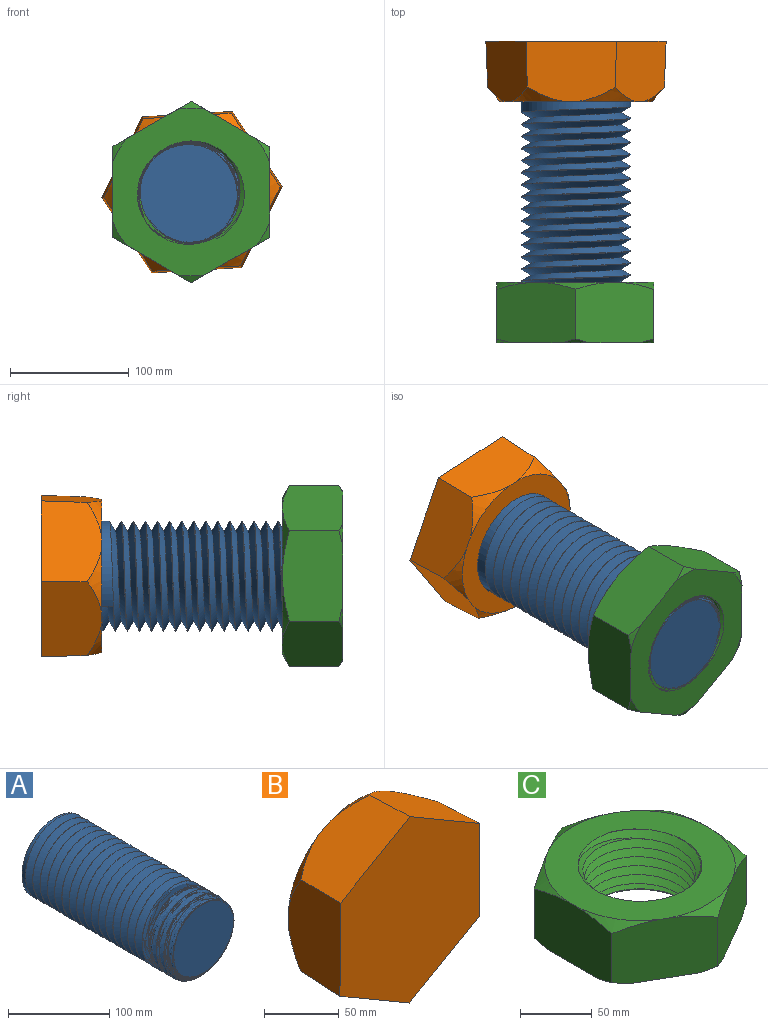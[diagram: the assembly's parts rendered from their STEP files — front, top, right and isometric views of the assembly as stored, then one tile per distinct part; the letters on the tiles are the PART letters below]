
ASSEMBLY  parts=3 mates=2
PART A: 6 faces, bbox 92.4x209.3x92.4 mm
  f0: cylinder r=46.22mm len=203.2mm, axis (0,-1,0), area 3392.6mm2, adj f1,f2,f3,f4,f5
  f1: plane 84.26x84.19mm, normal (0,-1,0), area 5573mm2, adj f0,f4,f5
  f2: plane 92.44x92.44mm, normal (0,1,0), area 6712mm2, adj f0
  f3: plane 9.91x8.58mm, normal (0,0,1), area 42.5mm2, adj f0,f4,f5
  f4: bspline ~204.34x92.44mm, area 50136.7mm2, adj f0,f1,f3,f5
  f5: bspline ~208.15x92.44mm, area 51491.4mm2, adj f0,f1,f3,f4
PART B: 14 faces, bbox 148.6x50.8x152.1 mm
  f0: plane 65.66x50.8mm, normal (-0.5,0.03,-0.86), area 3515.6mm2, adj f1,f5,f6,f7,f8,f13
  f1: plane 66.06x50.8mm, normal (0.5,0.03,-0.87), area 3515.6mm2, adj f0,f2,f6,f7,f12,f13
  f2: plane 76.04x50.8mm, normal (1,0.03,-0.01), area 3515.6mm2, adj f1,f3,f6,f7,f11,f12
  f3: plane 65.66x50.8mm, normal (0.5,0.03,0.86), area 3515.6mm2, adj f2,f4,f6,f7,f10,f11
  f4: plane 66.06x50.8mm, normal (-0.5,0.03,0.87), area 3515.6mm2, adj f3,f5,f6,f7,f9,f10
  f5: plane 76.04x50.8mm, normal (-1,0.03,0.01), area 3515.6mm2, adj f0,f4,f6,f7,f8,f9
  f6: plane 152.08x132.11mm, normal (0,-1,0), area 15023.2mm2, adj f0,f1,f2,f3,f4,f5
  f7: plane 128.55x128.21mm, normal (0,1,0), area 12971.7mm2, adj f0,f1,f2,f3,f4,f5,f8,f9
  f8: cone r=64.28mm half-angle=40.1deg, axis (0,-1,0), area 340.5mm2, adj f0,f5,f7
  f9: cone r=64.28mm half-angle=40.1deg, axis (0,-1,0), area 340.5mm2, adj f4,f5,f7
  f10: cone r=64.28mm half-angle=40.1deg, axis (0,-1,0), area 340.5mm2, adj f3,f4,f7
  f11: cone r=64.28mm half-angle=40.1deg, axis (0,-1,0), area 340.5mm2, adj f2,f3,f7
  f12: cone r=64.28mm half-angle=40.1deg, axis (0,-1,0), area 340.5mm2, adj f1,f2,f7
  f13: cone r=64.28mm half-angle=40.1deg, axis (0,-1,0), area 340.5mm2, adj f0,f1,f7
PART C: 24 faces, bbox 153.2x153.4x59.8 mm
  f0: plane 66.93x51.53mm, normal (-0.5,-0.87,0), area 3687.7mm2, adj f1,f5,f6,f7,f9,f10,f15,f19
  f1: plane 66.75x51.53mm, normal (0.5,-0.86,0), area 3687.7mm2, adj f0,f2,f6,f7,f8,f9,f18,f19
  f2: plane 77.08x51.54mm, normal (1,0,0), area 3687.7mm2, adj f1,f3,f6,f7,f8,f13,f17,f18
  f3: plane 66.93x51.53mm, normal (0.5,0.87,0), area 3687.7mm2, adj f2,f4,f6,f7,f12,f13,f16,f17
  f4: plane 66.75x51.53mm, normal (-0.5,0.86,0), area 3687.7mm2, adj f3,f5,f6,f7,f11,f12,f14,f16
  f5: plane 77.08x51.54mm, normal (-1,0,0), area 3687.7mm2, adj f0,f4,f6,f7,f10,f11,f14,f15
  f6: plane 142.18x133.02mm, normal (0,0,-1), area 8878.4mm2, adj f0,f1,f2,f3,f4,f5,f8,f9
  f7: plane 133.04x132.87mm, normal (0,0,1), area 7861.3mm2, adj f0,f1,f2,f3,f4,f5,f14,f15
  f8: cone r=94.64mm half-angle=60deg, axis (0,0,1), area 74.6mm2, adj f1,f2,f6
  f9: cone r=94.64mm half-angle=60deg, axis (0,0,1), area 74.6mm2, adj f0,f1,f6
  f10: cone r=94.64mm half-angle=60deg, axis (0,0,1), area 74.6mm2, adj f0,f5,f6
  f11: cone r=94.64mm half-angle=60deg, axis (0,0,1), area 74.6mm2, adj f4,f5,f6
  f12: cone r=94.64mm half-angle=60deg, axis (0,0,1), area 74.6mm2, adj f3,f4,f6
  f13: cone r=94.64mm half-angle=60deg, axis (0,0,1), area 74.6mm2, adj f2,f3,f6
  f14: cone r=94.64mm half-angle=60deg, axis (0,0,-1), area 264.2mm2, adj f4,f5,f7
  f15: cone r=94.64mm half-angle=60deg, axis (0,0,-1), area 264.2mm2, adj f0,f5,f7
  f16: cone r=94.64mm half-angle=60deg, axis (0,0,-1), area 264.2mm2, adj f3,f4,f7
  f17: cone r=94.64mm half-angle=60deg, axis (0,0,-1), area 264.2mm2, adj f2,f3,f7
  f18: cone r=94.64mm half-angle=60deg, axis (0,0,-1), area 264.2mm2, adj f1,f2,f7
  f19: cone r=94.64mm half-angle=60deg, axis (0,0,-1), area 264.2mm2, adj f0,f1,f7
  f20: cone r=37.95mm half-angle=45deg, axis (0,0,1), area 578.5mm2, adj f7,f22,f23
  f21: cone r=43.03mm half-angle=45deg, axis (0,0,-1), area 578.4mm2, adj f6,f22,f23
  f22: bspline ~90.17x90.17mm, area 12566.5mm2, adj f6,f7,f20,f21,f23
  f23: bspline ~90.17x90.17mm, area 12595.7mm2, adj f6,f7,f20,f21,f22
PLACE A rot(axis=(0,1,0),146.8deg) t=(176.46,122.07,-52.44)mm
PLACE B rot(axis=(-0.29,0,0.96),180deg) t=(176.46,122.07,-52.44)mm
PLACE C rot(axis=(0,-0.71,-0.71),180deg) t=(175.87,-81.13,-52.28)mm
MATE cylindrical A.f0 <-> B.f8  axis (0,1,0) through (176.46,122.07,-52.44)mm
MATE cylindrical A.f0 <-> C.f6  axis (0,-1,0) through (176.46,-81.13,-52.44)mm
